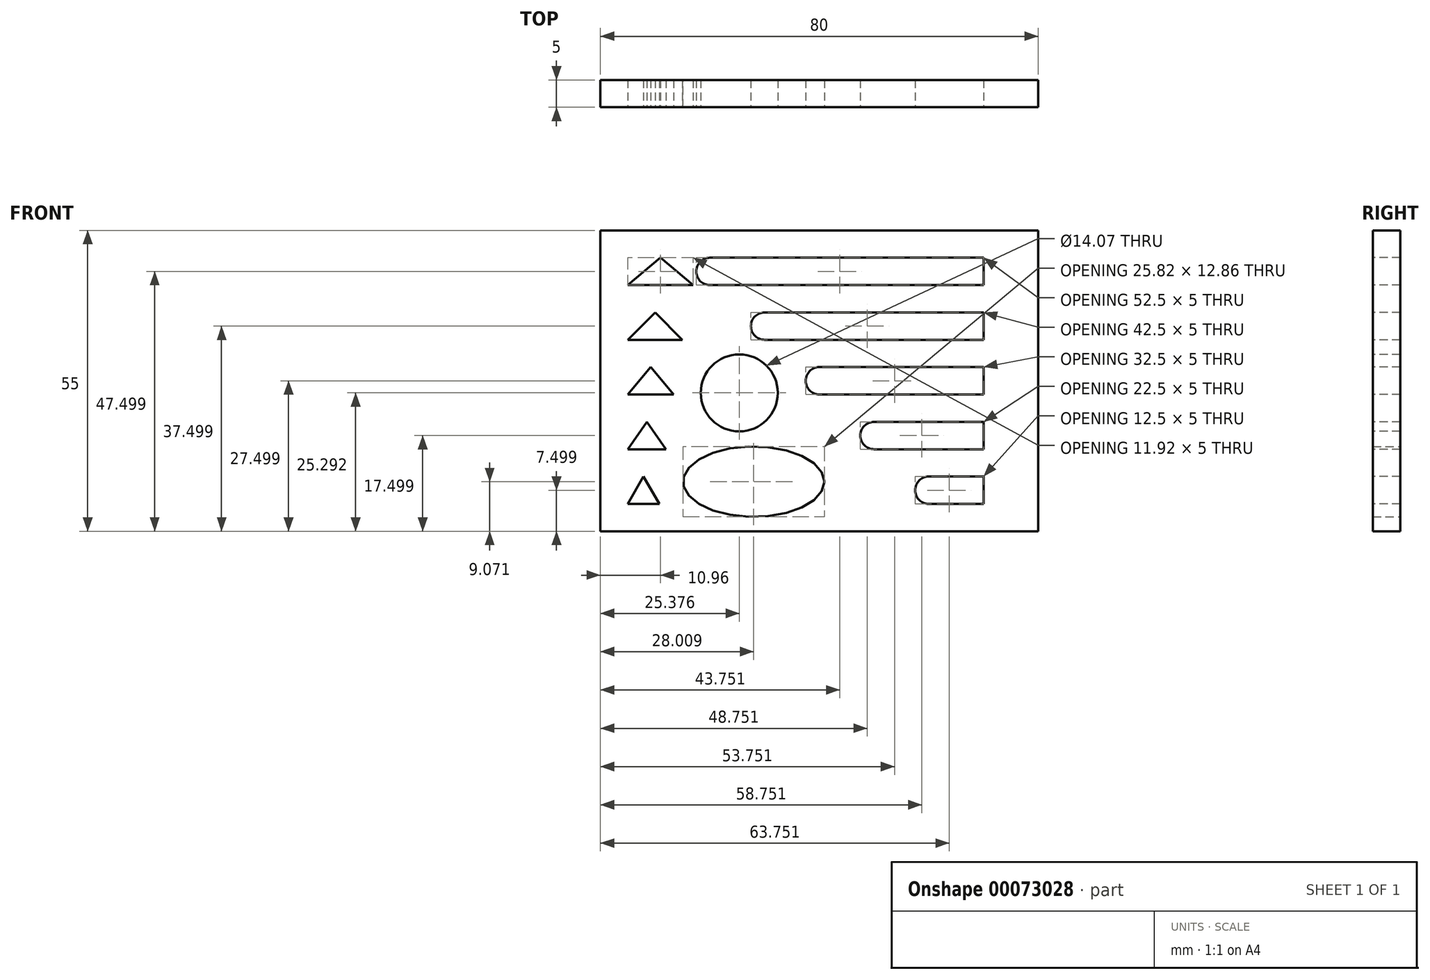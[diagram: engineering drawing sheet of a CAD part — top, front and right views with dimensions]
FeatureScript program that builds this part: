
annotation { "Feature Type Name" : "Feature", "Feature Type Description" : "" }
export const myFeature = defineFeature(function(context is Context, id is Id, definition is map)
    precondition{}
    {
        {
            var Q0;
            Q0=qCreatedBy(makeId("Front.planeOp"),FACE);
            var sketch = newSketch(context, id + "F0", { "sketchPlane" : qUnion([Q0])});
            skLineSegment(sketch, "E0.bottom", {"start": v(-46.04, 37.94) * mm, "end": v(33.96, 37.94) * mm});
            skLineSegment(sketch, "E0.top", {"start": v(-46.04, -17.06) * mm, "end": v(33.96, -17.06) * mm});
            skLineSegment(sketch, "E0.left", {"start": v(-46.04, 37.94) * mm, "end": v(-46.04, -17.06) * mm});
            skLineSegment(sketch, "E0.right", {"start": v(33.96, 37.94) * mm, "end": v(33.96, -17.06) * mm});
            skSolve(sketch);
        }
        {
            var Q0;
            Q0=makeQuery(id+"F0.imprint","IMPRINT",FACE,{"disambiguationData":[TD([[makeQuery(id+"F0.imprint","IMPRINT",EDGE,{"derivedFrom":sQuery(id+"F0.wireOp",EDGE,"E0.bottom")}),-1.0]])]});
            extrude(context, id + "F1", {"entities" : qUnion([Q0]), "depth" : 5 * mm});
        }
        {
            var Q0;
            Q0=makeQuery(id+"F1.opExtrude","CAP_FACE",FACE,{"disambiguationData":[OSD([sQuery(id+"F0.wireOp",EDGE,"E0.bottom"),sQuery(id+"F0.wireOp",EDGE,"E0.top"),sQuery(id+"F0.wireOp",EDGE,"E0.left"),sQuery(id+"F0.wireOp",EDGE,"E0.right")])],"isStart":false});
            var sketch = newSketch(context, id + "F2", { "sketchPlane" : qUnion([Q0])});
            skLineSegment(sketch, "E1.bottom", {"start": v(23.96, -12.06) * mm, "end": v(13.96, -12.06) * mm});
            skLineSegment(sketch, "E1.top", {"start": v(23.96, -7.06) * mm, "end": v(13.96, -7.06) * mm});
            skLineSegment(sketch, "E1.left", {"start": v(23.96, -12.06) * mm, "end": v(23.96, -7.06) * mm});
            skLineSegment(sketch, "E2.bottom", {"start": v(23.96, -2.06) * mm, "end": v(3.96, -2.06) * mm});
            skLineSegment(sketch, "E2.top", {"start": v(23.96, 2.94) * mm, "end": v(3.96, 2.94) * mm});
            skLineSegment(sketch, "E2.left", {"start": v(23.96, -2.06) * mm, "end": v(23.96, 2.94) * mm});
            skLineSegment(sketch, "E3.bottom", {"start": v(23.96, 7.94) * mm, "end": v(-6.04, 7.94) * mm});
            skLineSegment(sketch, "E3.top", {"start": v(23.96, 12.94) * mm, "end": v(-6.04, 12.94) * mm});
            skLineSegment(sketch, "E3.left", {"start": v(23.96, 7.94) * mm, "end": v(23.96, 12.94) * mm});
            skLineSegment(sketch, "E4.bottom", {"start": v(23.96, 17.94) * mm, "end": v(-16.04, 17.94) * mm});
            skLineSegment(sketch, "E4.top", {"start": v(23.96, 22.94) * mm, "end": v(-16.04, 22.94) * mm});
            skLineSegment(sketch, "E4.left", {"start": v(23.96, 17.94) * mm, "end": v(23.96, 22.94) * mm});
            skLineSegment(sketch, "E5.bottom", {"start": v(23.96, 27.94) * mm, "end": v(-26.04, 27.94) * mm});
            skLineSegment(sketch, "E5.top", {"start": v(23.96, 32.94) * mm, "end": v(-26.04, 32.94) * mm});
            skLineSegment(sketch, "E5.left", {"start": v(23.96, 27.94) * mm, "end": v(23.96, 32.94) * mm});
            skArc(sketch, "E6", {"start": v(-26.04, 32.94) * mm, "mid": v(-28.54, 30.44) * mm, "end": v(-26.04, 27.94) * mm});
            skArc(sketch, "E7", {"start": v(-16.04, 22.94) * mm, "mid": v(-18.54, 20.44) * mm, "end": v(-16.04, 17.94) * mm});
            skArc(sketch, "E8", {"start": v(-6.04, 12.94) * mm, "mid": v(-8.54, 10.44) * mm, "end": v(-6.04, 7.94) * mm});
            skArc(sketch, "E9", {"start": v(3.96, 2.94) * mm, "mid": v(1.46, 0.44) * mm, "end": v(3.96, -2.06) * mm});
            skArc(sketch, "E10", {"start": v(13.96, -7.06) * mm, "mid": v(11.46, -9.56) * mm, "end": v(13.96, -12.06) * mm});
            skSolve(sketch);
        }
        {
            var Q0;
            Q0 = qSketchRegion(id + "F2", true);
            extrude(context, id + "F3", {"entities" : qUnion([Q0]), "operationType" : NewBodyOperationType.REMOVE, "oppositeDirection" : true, "depth" : 25 * mm});
        }
        {
            var Q0;
            Q0=makeQuery(id+"F1.opExtrude","CAP_FACE",FACE,{"disambiguationData":[OSD([sQuery(id+"F0.wireOp",EDGE,"E0.bottom"),sQuery(id+"F0.wireOp",EDGE,"E0.top"),sQuery(id+"F0.wireOp",EDGE,"E0.left"),sQuery(id+"F0.wireOp",EDGE,"E0.right")])],"isStart":false});
            var sketch = newSketch(context, id + "F4", { "sketchPlane" : qUnion([Q0])});
            skLineSegment(sketch, "E11", {"start": v(-41.04, -12.06) * mm, "end": v(-38.15, -7.06) * mm});
            skLineSegment(sketch, "E12", {"start": v(-41.04, -2.06) * mm, "end": v(-37.54, 2.94) * mm});
            skLineSegment(sketch, "E13", {"start": v(-41.04, 7.94) * mm, "end": v(-36.84, 12.94) * mm});
            skLineSegment(sketch, "E14", {"start": v(-41.04, 17.94) * mm, "end": v(-36.04, 22.94) * mm});
            skLineSegment(sketch, "E15", {"start": v(-41.04, 27.94) * mm, "end": v(-35.08, 32.94) * mm});
            skLineSegment(sketch, "E16", {"start": v(-35.08, 27.94) * mm, "end": v(-41.04, 27.94) * mm});
            skLineSegment(sketch, "E17", {"start": v(-36.04, 17.94) * mm, "end": v(-41.04, 17.94) * mm});
            skLineSegment(sketch, "E18", {"start": v(-36.84, 7.94) * mm, "end": v(-41.04, 7.94) * mm});
            skLineSegment(sketch, "E19", {"start": v(-37.54, -2.06) * mm, "end": v(-41.04, -2.06) * mm});
            skLineSegment(sketch, "E20", {"start": v(-38.15, -12.06) * mm, "end": v(-41.04, -12.06) * mm});
            skLineSegment(sketch, "E21.MirrorCS", {"start": v(-29.12, 27.94) * mm, "end": v(-35.08, 32.94) * mm});
            skLineSegment(sketch, "E22.MirrorCS", {"start": v(-35.08, 27.94) * mm, "end": v(-29.12, 27.94) * mm});
            skLineSegment(sketch, "E23.MirrorCS", {"start": v(-31.04, 17.94) * mm, "end": v(-36.04, 22.94) * mm});
            skLineSegment(sketch, "E24.MirrorCS", {"start": v(-36.04, 17.94) * mm, "end": v(-31.04, 17.94) * mm});
            skLineSegment(sketch, "E25.MirrorCS", {"start": v(-32.65, 7.94) * mm, "end": v(-36.84, 12.94) * mm});
            skLineSegment(sketch, "E26.MirrorCS", {"start": v(-36.84, 7.94) * mm, "end": v(-32.65, 7.94) * mm});
            skLineSegment(sketch, "E27.MirrorCS", {"start": v(-34.04, -2.06) * mm, "end": v(-37.54, 2.94) * mm});
            skLineSegment(sketch, "E28.MirrorCS", {"start": v(-37.54, -2.06) * mm, "end": v(-34.04, -2.06) * mm});
            skLineSegment(sketch, "E29.MirrorCS", {"start": v(-35.27, -12.06) * mm, "end": v(-38.15, -7.06) * mm});
            skLineSegment(sketch, "E30.MirrorCS", {"start": v(-38.15, -12.06) * mm, "end": v(-35.27, -12.06) * mm});
            skSolve(sketch);
        }
        {
            var Q0;
            Q0 = qSketchRegion(id + "F4", true);
            extrude(context, id + "F5", {"entities" : qUnion([Q0]), "operationType" : NewBodyOperationType.REMOVE, "oppositeDirection" : true, "depth" : 10 * mm});
        }
        {
            var Q0;
            Q0=makeQuery(id+"F1.opExtrude","CAP_FACE",FACE,{"disambiguationData":[OSD([sQuery(id+"F0.wireOp",EDGE,"E0.bottom"),sQuery(id+"F0.wireOp",EDGE,"E0.top"),sQuery(id+"F0.wireOp",EDGE,"E0.left"),sQuery(id+"F0.wireOp",EDGE,"E0.right")])],"isStart":false});
            var sketch = newSketch(context, id + "F6", { "sketchPlane" : qUnion([Q0])});
            skCircle(sketch, "E31", {"center": v(-20.66, 8.23) * mm, "radius": 7.04 * mm});
            skEllipse(sketch, "E32", {"center": v(-18.03, -7.99) * mm, "majorRadius": 12.9 * mm, "minorRadius": 6.43 * mm, "majorAxis": v(1, 0)});
            skSolve(sketch);
        }
        {
            var Q0;
            Q0 = qSketchRegion(id + "F6", true);
            extrude(context, id + "F7", {"entities" : qUnion([Q0]), "operationType" : NewBodyOperationType.REMOVE, "oppositeDirection" : true, "depth" : 10 * mm});
        }
    });
